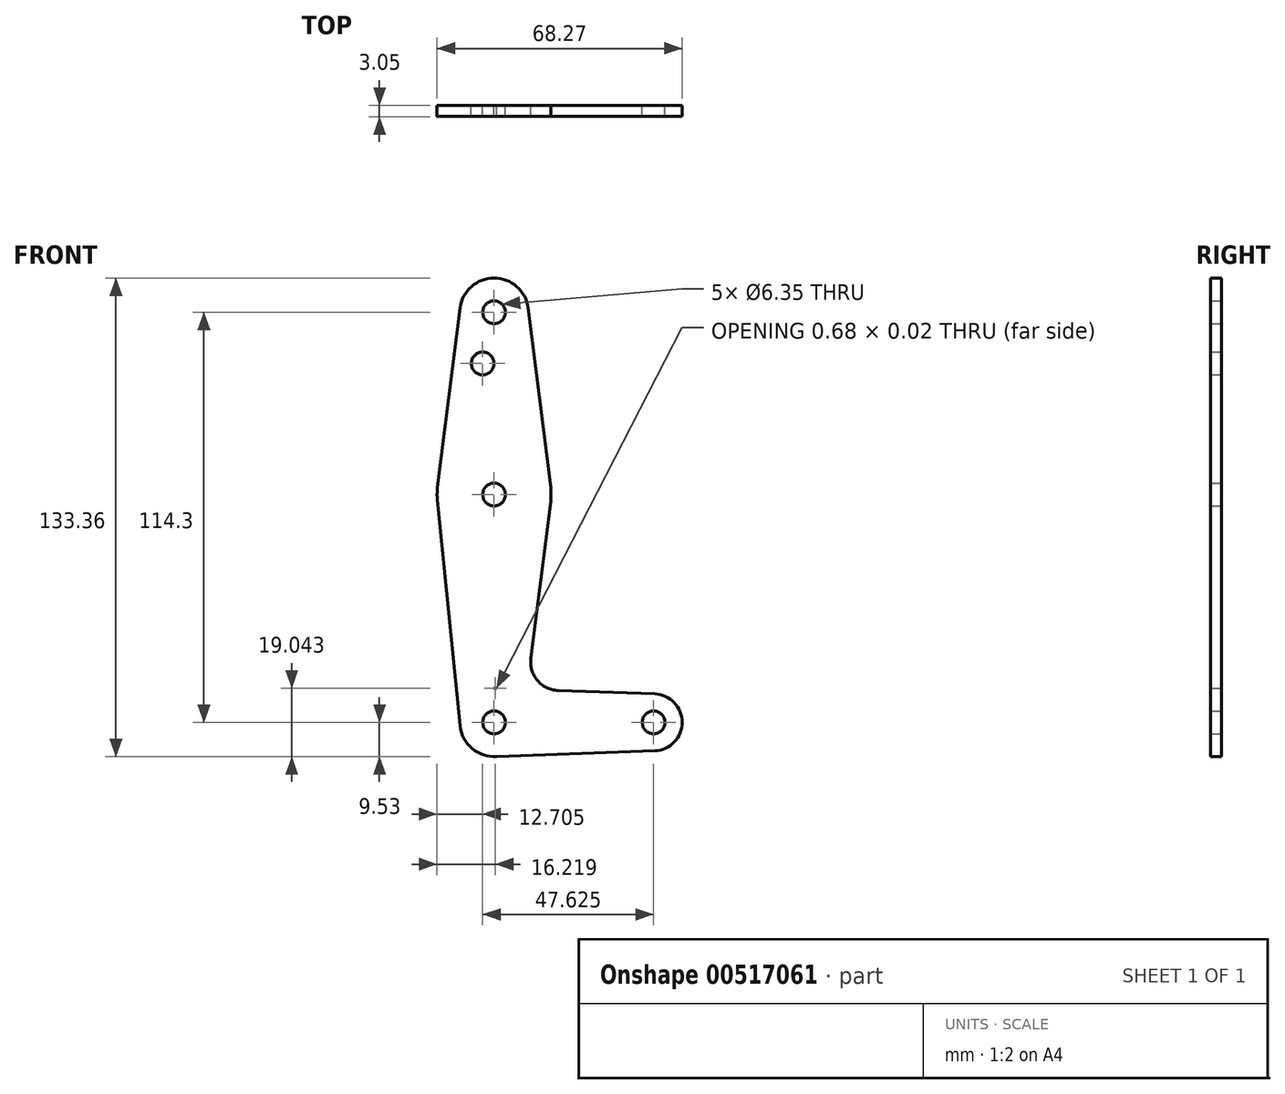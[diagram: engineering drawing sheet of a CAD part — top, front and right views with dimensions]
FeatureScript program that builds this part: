
annotation { "Feature Type Name" : "Feature", "Feature Type Description" : "" }
export const myFeature = defineFeature(function(context is Context, id is Id, definition is map)
    precondition{}
    {
        {
            var Q0;
            Q0=qCreatedBy(makeId("Front.planeOp"),FACE);
            var sketch = newSketch(context, id + "F0", { "sketchPlane" : qUnion([Q0])});
            skCircle(sketch, "E0", {"center": v(0, 114.3) * mm, "radius": 9.53 * mm});
            skCircle(sketch, "E1", {"center": v(0, 0) * mm, "radius": 9.53 * mm});
            skCircle(sketch, "E2", {"center": v(44.45, 0) * mm, "radius": 7.94 * mm});
            skCircle(sketch, "E3", {"center": v(0, 63.5) * mm, "radius": 15.88 * mm});
            skLineSegment(sketch, "E4", {"start": v(-9.45, 115.5) * mm, "end": v(-15.75, 65.48) * mm});
            skLineSegment(sketch, "E5", {"start": v(9.45, 115.5) * mm, "end": v(15.75, 65.48) * mm});
            skCircle(sketch, "E6", {"center": v(0, 114.3) * mm, "radius": 3.18 * mm});
            skCircle(sketch, "E7", {"center": v(0, 63.5) * mm, "radius": 3.18 * mm});
            skCircle(sketch, "E8", {"center": v(0, 0) * mm, "radius": 3.18 * mm});
            skCircle(sketch, "E9", {"center": v(44.45, 0) * mm, "radius": 3.18 * mm});
            skCircle(sketch, "E10", {"center": v(-3.17, 100.03) * mm, "radius": 3.18 * mm});
            skLineSegment(sketch, "E11", {"start": v(0, 114.3) * mm, "end": v(0, 63.5) * mm, "construction": true});
            skLineSegment(sketch, "E12", {"start": v(0, 0) * mm, "end": v(0, 63.5) * mm, "construction": true});
            skLineSegment(sketch, "E13", {"start": v(0, 0) * mm, "end": v(44.45, 0) * mm, "construction": true});
            skPoint(sketch, "E14.end.orphan", {"position": v(-9.57, 0) * mm});
            skLineSegment(sketch, "E15", {"start": v(-15.8, 61.91) * mm, "end": v(-9.48, -0.95) * mm});
            skLineSegment(sketch, "E16", {"start": v(0, 9.52) * mm, "end": v(0.68, 9.5) * mm});
            skLineSegment(sketch, "E17", {"start": v(0, -9.52) * mm, "end": v(44.73, -7.93) * mm});
            skPoint(sketch, "E18.end.orphan", {"position": v(5.27, 7.93) * mm});
            skPoint(sketch, "E19.orphan", {"position": v(44.73, 7.93) * mm});
            skLineSegment(sketch, "E20", {"start": v(15.75, 61.52) * mm, "end": v(10.25, 17.83) * mm});
            skLineSegment(sketch, "E21", {"start": v(17.85, 8.9) * mm, "end": v(44.73, 7.93) * mm});
            skArc(sketch, "E22.filletArc", {"start": v(10.25, 17.83) * mm, "mid": v(12.08, 11.69) * mm, "end": v(17.85, 8.9) * mm});
            skSolve(sketch);
        }
        {
            var Q0;
            Q0=qSketchRegion(id+"F0",true);
            extrude(context, id + "F1", {"entities" : qUnion([Q0]), "depth" : 3.05 * mm, "offsetDistance" : 25.4 * mm});
        }
    });
